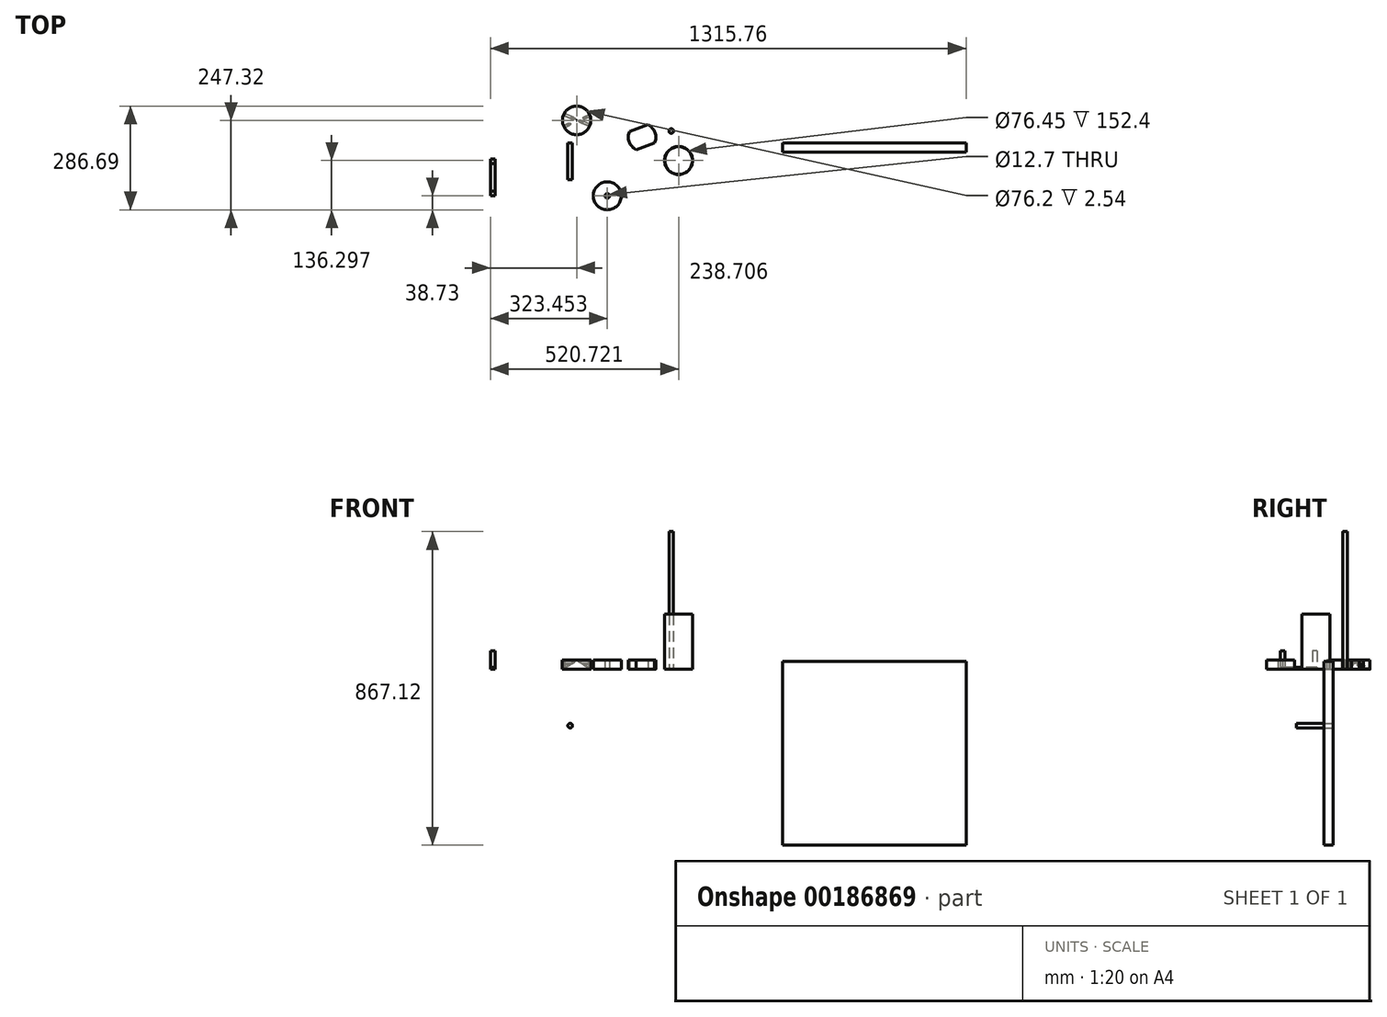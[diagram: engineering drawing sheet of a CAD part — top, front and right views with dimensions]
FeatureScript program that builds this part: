
annotation { "Feature Type Name" : "Feature", "Feature Type Description" : "" }
export const myFeature = defineFeature(function(context is Context, id is Id, definition is map)
    precondition{}
    {
        {
            var Q0;
            Q0=qCreatedBy(makeId("Top.planeOp"),FACE);
            var sketch = newSketch(context, id + "F0", { "sketchPlane" : qUnion([Q0])});
            skArc(sketch, "E0", {"start": v(-71.55, 32.72) * mm, "mid": v(-73.04, 3.6) * mm, "end": v(-53.5, -18.05) * mm});
            skLineSegment(sketch, "E1", {"start": v(-37.14, 16.36) * mm, "end": v(-2.73, 0) * mm});
            skLineSegment(sketch, "E2", {"start": v(-37.14, 16.36) * mm, "end": v(-53.5, -18.05) * mm});
            skLineSegment(sketch, "E3", {"start": v(-53.5, -18.05) * mm, "end": v(-2.73, 0) * mm});
            skLineSegment(sketch, "E4", {"start": v(-37.14, 16.36) * mm, "end": v(-20.78, 50.77) * mm});
            skLineSegment(sketch, "E5", {"start": v(-37.14, 16.36) * mm, "end": v(-71.55, 32.72) * mm});
            skLineSegment(sketch, "E6", {"start": v(-71.55, 32.72) * mm, "end": v(-20.78, 50.77) * mm});
            skArc(sketch, "E7.trimOffspring", {"start": v(-2.73, 0) * mm, "mid": v(-1.24, 29.12) * mm, "end": v(-20.78, 50.77) * mm});
            skSolve(sketch);
        }
        {
            var Q0;
            Q0=makeQuery(id+"F0.imprint","IMPRINT",FACE,{"disambiguationData":[TD([[makeQuery(id+"F0.imprint","IMPRINT",EDGE,{"derivedFrom":sQuery(id+"F0.wireOp",EDGE,"E1")}),1.0]])]});
            var Q1;
            Q1=makeQuery(id+"F0.imprint","IMPRINT",FACE,{"disambiguationData":[TD([[makeQuery(id+"F0.imprint","IMPRINT",EDGE,{"derivedFrom":sQuery(id+"F0.wireOp",EDGE,"E1")}),-1.0]])]});
            var Q2;
            Q2=makeQuery(id+"F0.imprint","IMPRINT",FACE,{"disambiguationData":[TD([[makeQuery(id+"F0.imprint","IMPRINT",EDGE,{"derivedFrom":sQuery(id+"F0.wireOp",EDGE,"E0")}),1.0]])]});
            var Q3;
            Q3=makeQuery(id+"F0.imprint","IMPRINT",FACE,{"disambiguationData":[TD([[makeQuery(id+"F0.imprint","IMPRINT",EDGE,{"derivedFrom":sQuery(id+"F0.wireOp",EDGE,"E4")}),1.0]])]});
            extrude(context, id + "F1", {"entities" : qUnion([Q0, Q1, Q2, Q3]), "depth" : 25.4 * mm});
        }
        {
            var Q0;
            Q0=qCreatedBy(makeId("Top.planeOp"),FACE);
            var sketch = newSketch(context, id + "F2", { "sketchPlane" : qUnion([Q0])});
            skCircle(sketch, "E8", {"center": v(63.96, -48.2) * mm, "radius": 38.74 * mm});
            skLineSegment(sketch, "E9", {"start": v(63.96, -48.2) * mm, "end": v(77.82, -12.02) * mm});
            skLineSegment(sketch, "E10", {"start": v(63.96, -48.2) * mm, "end": v(43.71, -81.21) * mm});
            skSolve(sketch);
        }
        {
            var Q0;
            Q0=makeQuery(id+"F2.imprint","IMPRINT",FACE,{"disambiguationData":[TD([[makeQuery(id+"F2.imprint","IMPRINT",EDGE,{"derivedFrom":sQuery(id+"F2.wireOp",EDGE,"E8")}),1.0]])]});
            extrude(context, id + "F3", {"entities" : qUnion([Q0]), "depth" : 152.4 * mm});
        }
        {
            var Q0;
            Q0=makeQuery(id+"F3.opExtrude","CAP_FACE",FACE,{"disambiguationData":[OSD([sQuery(id+"F2.wireOp",EDGE,"E8")])],"isStart":false});
            var sketch = newSketch(context, id + "F4", { "sketchPlane" : qUnion([Q0])});
            skLineSegment(sketch, "E11", {"start": v(63.96, -48.2) * mm, "end": v(77.44, -11.88) * mm});
            skSolve(sketch);
        }
        {
            var Q0;
            Q0=sQuery(id+"F4.wireOp",VERTEX,"E11.start");
            var Q1;
            Q1=makeQuery(id+"F3.opExtrude","SWEPT_BODY",BODY,{"disambiguationData":[OSD([sQuery(id+"F2.wireOp",EDGE,"E8")])]});
            hole(context, id + "F5", {"style" : HoleStyle.SIMPLE, "endStyle" : HoleEndStyle.BLIND, "holeDiameter" : 76.45 * mm, "holeDepth" : 152.4 * mm, "locations" : qUnion([Q0]), "scope" : qUnion([Q1])});
        }
        {
            var Q0;
            Q0=qCreatedBy(makeId("Top.planeOp"),FACE);
            var sketch = newSketch(context, id + "F6", { "sketchPlane" : qUnion([Q0])});
            skCircle(sketch, "E12", {"center": v(-133.3, -145.76) * mm, "radius": 38.73 * mm});
            skCircle(sketch, "E13", {"center": v(-133.3, -145.76) * mm, "radius": 6.35 * mm});
            skSolve(sketch);
        }
        {
            var Q0;
            Q0=qCreatedBy(makeId("Top.planeOp"),FACE);
            var sketch = newSketch(context, id + "F7", { "sketchPlane" : qUnion([Q0])});
            skCircle(sketch, "E14", {"center": v(43.56, 33.42) * mm, "radius": 6.22 * mm});
            skSolve(sketch);
        }
        {
            var Q0;
            Q0=makeQuery(id+"F7.imprint","IMPRINT",FACE,{"disambiguationData":[TD([[makeQuery(id+"F7.imprint","IMPRINT",EDGE,{"derivedFrom":sQuery(id+"F7.wireOp",EDGE,"E14")}),1.0]])]});
            extrude(context, id + "F8", {"entities" : qUnion([Q0]), "depth" : 381 * mm});
        }
        {
            var Q0;
            Q0=makeQuery(id+"F6.imprint","IMPRINT",FACE,{"disambiguationData":[TD([[makeQuery(id+"F6.imprint","IMPRINT",EDGE,{"derivedFrom":sQuery(id+"F6.wireOp",EDGE,"E12")}),1.0]])]});
            extrude(context, id + "F9", {"entities" : qUnion([Q0]), "depth" : 25.4 * mm});
        }
        {
            var Q0;
            Q0=qCreatedBy(makeId("Top.planeOp"),FACE);
            var sketch = newSketch(context, id + "F10", { "sketchPlane" : qUnion([Q0])});
            skCircle(sketch, "E15", {"center": v(-218.05, 62.83) * mm, "radius": 39.37 * mm});
            skLineSegment(sketch, "E16", {"start": v(-184.55, 83.5) * mm, "end": v(-179.7, 71.74) * mm});
            skLineSegment(sketch, "E17", {"start": v(-179.7, 71.74) * mm, "end": v(-256.4, 71.74) * mm});
            skLineSegment(sketch, "E18", {"start": v(-184.55, 83.5) * mm, "end": v(-251.56, 83.5) * mm});
            skLineSegment(sketch, "E19", {"start": v(-251.56, 83.5) * mm, "end": v(-256.4, 71.74) * mm});
            skSolve(sketch);
        }
        {
            var Q0;
            {var subQ0=sQuery(id+"F10.wireOp",EDGE,"E17");Q0=makeQuery(id+"F10.imprint","IMPRINT",FACE,{"disambiguationData":[TD([[makeQuery(id+"F10.imprint","IMPRINT",EDGE,{"derivedFrom":subQ0}),1.0]])]});}
            var Q1;
            {var subQ0=sQuery(id+"F10.wireOp",EDGE,"E18");Q1=makeQuery(id+"F10.imprint","IMPRINT",FACE,{"disambiguationData":[TD([[makeQuery(id+"F10.imprint","IMPRINT",EDGE,{"derivedFrom":subQ0}),-1.0]])]});}
            var Q2;
            Q2=makeQuery(id+"F10.imprint","IMPRINT",FACE,{"disambiguationData":[TD([[makeQuery(id+"F10.imprint","IMPRINT",EDGE,{"derivedFrom":sQuery(id+"F10.wireOp",EDGE,"E16")}),-1.0]])]});
            extrude(context, id + "F11", {"entities" : qUnion([Q0, Q1, Q2]), "depth" : 25.4 * mm});
        }
        {
            var Q0;
            Q0=makeQuery(id+"F11.opExtrude","SWEPT_FACE",FACE,{"disambiguationData":[OSD([sQuery(id+"F10.wireOp",EDGE,"E16")])]});
            var sketch = newSketch(context, id + "F12", { "sketchPlane" : qUnion([Q0])});
            skCircle(sketch, "E20", {"center": v(139.33, 10.9) * mm, "radius": 2.55 * mm});
            skSolve(sketch);
        }
        {
            var Q0;
            Q0=makeQuery(id+"F11.opExtrude","SWEPT_FACE",FACE,{"disambiguationData":[OSD([sQuery(id+"F10.wireOp",EDGE,"E19")])]});
            var sketch = newSketch(context, id + "F13", { "sketchPlane" : qUnion([Q0])});
            skCircle(sketch, "E21", {"center": v(23.53, 18.47) * mm, "radius": 3.6 * mm});
            skSolve(sketch);
        }
        {
            var Q0;
            Q0=sQuery(id+"F13.wireOp",VERTEX,"E21.center");
            var Q1;
            Q1=makeQuery(id+"F11.opExtrude","SWEPT_BODY",BODY,{"disambiguationData":[OSD([sQuery(id+"F10.wireOp",EDGE,"E15"),sQuery(id+"F10.wireOp",EDGE,"E16"),sQuery(id+"F10.wireOp",EDGE,"E19")])]});
            hole(context, id + "F14", {"style" : HoleStyle.SIMPLE, "endStyle" : HoleEndStyle.BLIND, "holeDiameter" : 6.35 * mm, "holeDepth" : 76.2 * mm, "locations" : qUnion([Q0]), "scope" : qUnion([Q1])});
        }
        {
            var Q0;
            Q0=sQuery(id+"F12.wireOp",VERTEX,"E20.center");
            var Q1;
            Q1=makeQuery(id+"F11.opExtrude","SWEPT_BODY",BODY,{"disambiguationData":[OSD([sQuery(id+"F10.wireOp",EDGE,"E15"),sQuery(id+"F10.wireOp",EDGE,"E16"),sQuery(id+"F10.wireOp",EDGE,"E19")])]});
            hole(context, id + "F15", {"style" : HoleStyle.SIMPLE, "endStyle" : HoleEndStyle.BLIND, "holeDiameter" : 6.35 * mm, "holeDepth" : 76.2 * mm, "locations" : qUnion([Q0]), "scope" : qUnion([Q1])});
        }
        {
            var Q0;
            Q0=makeQuery(id+"F11.opExtrude","CAP_FACE",FACE,{"disambiguationData":[OSD([sQuery(id+"F10.wireOp",EDGE,"E15"),sQuery(id+"F10.wireOp",EDGE,"E16"),sQuery(id+"F10.wireOp",EDGE,"E19")])],"isStart":true});
            var sketch = newSketch(context, id + "F16", { "sketchPlane" : qUnion([Q0])});
            skLineSegment(sketch, "E22", {"start": v(-218.05, -62.83) * mm, "end": v(-246.75, -35.88) * mm});
            skSolve(sketch);
        }
        {
            var Q0;
            Q0=sQuery(id+"F16.wireOp",VERTEX,"E22.start");
            var Q1;
            Q1=makeQuery(id+"F11.opExtrude","SWEPT_BODY",BODY,{"disambiguationData":[OSD([sQuery(id+"F10.wireOp",EDGE,"E15"),sQuery(id+"F10.wireOp",EDGE,"E16"),sQuery(id+"F10.wireOp",EDGE,"E19")])]});
            hole(context, id + "F17", {"style" : HoleStyle.SIMPLE, "endStyle" : HoleEndStyle.BLIND, "holeDiameter" : 76.2 * mm, "holeDepth" : 2.54 * mm, "locations" : qUnion([Q0]), "scope" : qUnion([Q1])});
        }
        {
            var Q0;
            Q0=qCreatedBy(makeId("Front.planeOp"),FACE);
            var sketch = newSketch(context, id + "F18", { "sketchPlane" : qUnion([Q0])});
            skCircle(sketch, "E23", {"center": v(-235.99, -155.5) * mm, "radius": 6.35 * mm});
            skSolve(sketch);
        }
        {
            var Q0;
            Q0=makeQuery(id+"F18.imprint","IMPRINT",FACE,{"disambiguationData":[TD([[makeQuery(id+"F18.imprint","IMPRINT",EDGE,{"derivedFrom":sQuery(id+"F18.wireOp",EDGE,"E23")}),1.0]])]});
            extrude(context, id + "F19", {"entities" : qUnion([Q0]), "depth" : 101.6 * mm});
        }
        {
            var Q0;
            Q0=qCreatedBy(makeId("Top.planeOp"),FACE);
            var sketch = newSketch(context, id + "F20", { "sketchPlane" : qUnion([Q0])});
            skLineSegment(sketch, "E24.bottom", {"start": v(-444.06, -44.38) * mm, "end": v(-456.76, -44.38) * mm});
            skLineSegment(sketch, "E24.top", {"start": v(-444.06, -145.98) * mm, "end": v(-456.76, -145.98) * mm});
            skLineSegment(sketch, "E24.left", {"start": v(-444.06, -44.38) * mm, "end": v(-444.06, -145.98) * mm});
            skLineSegment(sketch, "E24.right", {"start": v(-456.76, -44.38) * mm, "end": v(-456.76, -145.98) * mm});
            skLineSegment(sketch, "E25", {"start": v(-444.06, -57.08) * mm, "end": v(-456.76, -57.08) * mm});
            skLineSegment(sketch, "E26", {"start": v(-444.06, -57.08) * mm, "end": v(-444.06, -44.38) * mm});
            skLineSegment(sketch, "E27", {"start": v(-456.76, -44.38) * mm, "end": v(-456.76, -57.08) * mm});
            skLineSegment(sketch, "E28", {"start": v(-444.06, -133.28) * mm, "end": v(-456.76, -133.28) * mm});
            skLineSegment(sketch, "E29", {"start": v(-456.76, -133.28) * mm, "end": v(-456.76, -145.98) * mm});
            skLineSegment(sketch, "E30", {"start": v(-444.06, -145.98) * mm, "end": v(-444.06, -133.28) * mm});
            skSolve(sketch);
        }
        {
            var Q0;
            Q0=makeQuery(id+"F20.imprint","IMPRINT",FACE,{"disambiguationData":[TD([[makeQuery(id+"F20.imprint","IMPRINT",EDGE,{"derivedFrom":sQuery(id+"F20.wireOp",EDGE,"E24.bottom")}),1.0]])]});
            var Q1;
            Q1=makeQuery(id+"F20.imprint","IMPRINT",FACE,{"disambiguationData":[TD([[makeQuery(id+"F20.imprint","IMPRINT",EDGE,{"derivedFrom":sQuery(id+"F20.wireOp",EDGE,"E24.top")}),-1.0]])]});
            extrude(context, id + "F21", {"entities" : qUnion([Q0, Q1]), "depth" : 50.8 * mm});
        }
        {
            var Q0;
            Q0 = qSketchRegion(id + "F20", true);
            extrude(context, id + "F22", {"entities" : qUnion([Q0]), "depth" : 5.08 * mm});
        }
        {
            var Q0;
            Q0=qCreatedBy(makeId("Front.planeOp"),FACE);
            var sketch = newSketch(context, id + "F23", { "sketchPlane" : qUnion([Q0])});
            skLineSegment(sketch, "E31.bottom", {"start": v(351, 21.88) * mm, "end": v(859, 21.88) * mm});
            skLineSegment(sketch, "E31.top", {"start": v(351, -486.12) * mm, "end": v(859, -486.12) * mm});
            skLineSegment(sketch, "E31.left", {"start": v(351, 21.88) * mm, "end": v(351, -486.12) * mm});
            skLineSegment(sketch, "E31.right", {"start": v(859, 21.88) * mm, "end": v(859, -486.12) * mm});
            skSolve(sketch);
        }
        {
            var Q0;
            Q0=makeQuery(id+"F23.imprint","IMPRINT",FACE,{"disambiguationData":[TD([[makeQuery(id+"F23.imprint","IMPRINT",EDGE,{"derivedFrom":sQuery(id+"F23.wireOp",EDGE,"E31.bottom")}),-1.0]])]});
            extrude(context, id + "F24", {"entities" : qUnion([Q0]), "depth" : 25.4 * mm});
        }
    });
